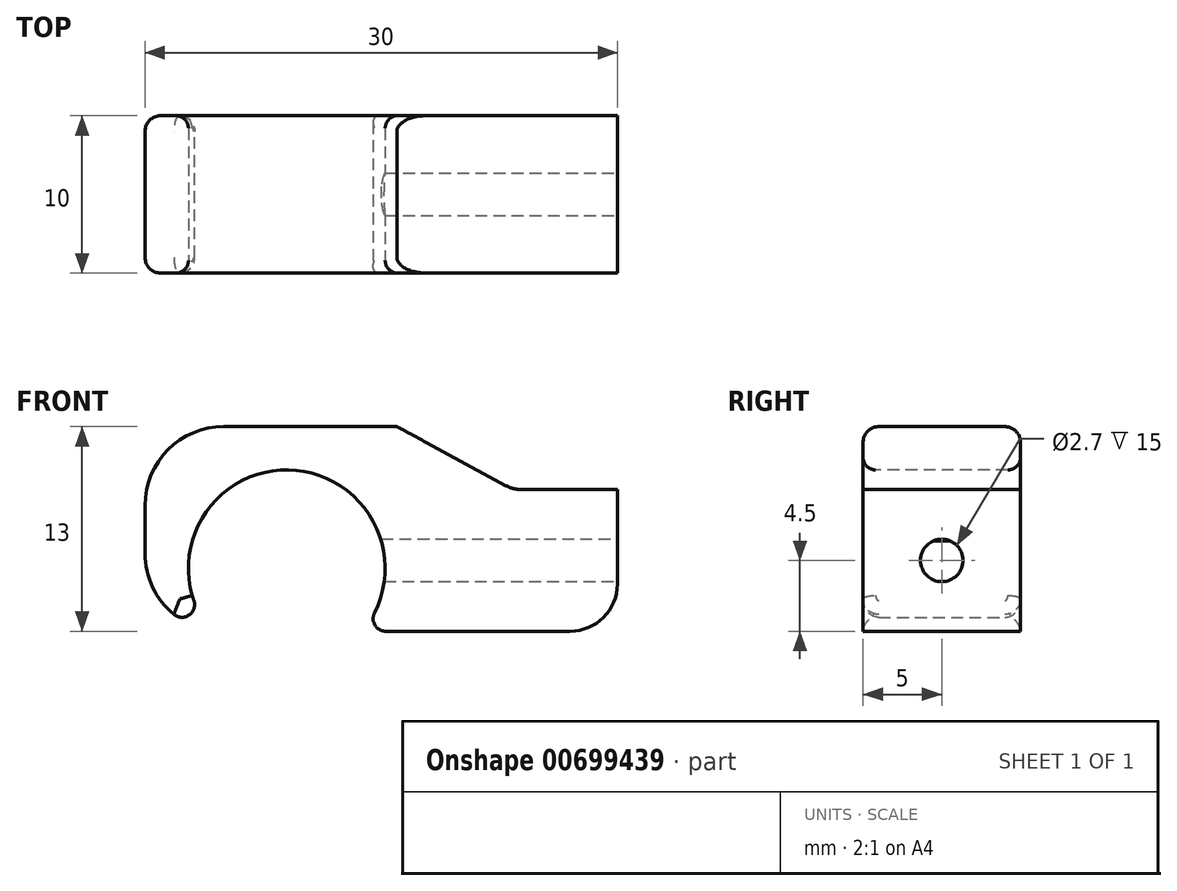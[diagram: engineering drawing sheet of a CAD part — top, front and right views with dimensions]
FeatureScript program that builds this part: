
annotation { "Feature Type Name" : "Feature", "Feature Type Description" : "" }
export const myFeature = defineFeature(function(context is Context, id is Id, definition is map)
    precondition{}
    {
        {
            var Q0;
            Q0=qCreatedBy(makeId("Top.planeOp"),FACE);
            var sketch = newSketch(context, id + "F0", { "sketchPlane" : qUnion([Q0])});
            skLineSegment(sketch, "E0.bottom", {"start": v(-15, 5) * mm, "end": v(15, 5) * mm});
            skLineSegment(sketch, "E0.top", {"start": v(-15, -5) * mm, "end": v(15, -5) * mm});
            skLineSegment(sketch, "E0.left", {"start": v(-15, 5) * mm, "end": v(-15, -5) * mm});
            skLineSegment(sketch, "E0.right", {"start": v(15, 5) * mm, "end": v(15, -5) * mm});
            skSolve(sketch);
        }
        {
            var Q0;
            Q0=makeQuery(id+"F0.imprint","IMPRINT",FACE,{"disambiguationData":[TD([[makeQuery(id+"F0.imprint","IMPRINT",EDGE,{"derivedFrom":sQuery(id+"F0.wireOp",EDGE,"E0.bottom")}),-1.0]])]});
            extrude(context, id + "F1", {"entities" : qUnion([Q0]), "depth" : 13 * mm, "offsetDistance" : 25 * mm});
        }
        {
            var Q0;
            Q0=makeQuery(id+"F1.opExtrude","SWEPT_FACE",FACE,{"disambiguationData":[OSD([sQuery(id+"F0.wireOp",EDGE,"E0.top")])]});
            var sketch = newSketch(context, id + "F2", { "sketchPlane" : qUnion([Q0])});
            skCircle(sketch, "E1", {"center": v(-6, 4) * mm, "radius": 6.25 * mm});
            skSolve(sketch);
        }
        {
            var Q0;
            Q0 = qSketchRegion(id + "F2", true);
            extrude(context, id + "F3", {"entities" : qUnion([Q0]), "operationType" : NewBodyOperationType.REMOVE, "endBound" : BoundingType.THROUGH_ALL, "oppositeDirection" : true, "depth" : 25 * mm, "offsetDistance" : 25 * mm});
        }
        {
            var Q0;
            Q0=makeQuery(id+"F1.opExtrude","CAP_EDGE",EDGE,{"disambiguationData":[OSD([sQuery(id+"F0.wireOp",EDGE,"E0.left")])],"isStart":false});
            var Q1;
            Q1=makeQuery(id+"F1.opExtrude","CAP_EDGE",EDGE,{"disambiguationData":[OSD([sQuery(id+"F0.wireOp",EDGE,"E0.left")])],"isStart":true});
            fillet(context, id + "F4", {"entities" : qUnion([Q0, Q1]), "radius" : 5 * mm, "tangentPropagation" : true, "allowEdgeOverflow" : false});
        }
        {
            var Q0;
            Q0=makeQuery(id+"F1.opExtrude","SWEPT_FACE",FACE,{"disambiguationData":[OSD([sQuery(id+"F0.wireOp",EDGE,"E0.top")])]});
            var sketch = newSketch(context, id + "F5", { "sketchPlane" : qUnion([Q0])});
            skLineSegment(sketch, "E2.bottom", {"start": v(15, 13) * mm, "end": v(1, 13) * mm});
            skLineSegment(sketch, "E2.top", {"start": v(15, 9) * mm, "end": v(8.38, 9) * mm});
            skLineSegment(sketch, "E2.left", {"start": v(15, 13) * mm, "end": v(15, 9) * mm});
            skLineSegment(sketch, "E3", {"start": v(1, 13) * mm, "end": v(8.38, 9) * mm});
            skSolve(sketch);
        }
        {
            var Q0;
            Q0 = qSketchRegion(id + "F5", true);
            extrude(context, id + "F6", {"entities" : qUnion([Q0]), "operationType" : NewBodyOperationType.REMOVE, "endBound" : BoundingType.THROUGH_ALL, "oppositeDirection" : true, "depth" : 25 * mm, "offsetDistance" : 25 * mm});
        }
        {
            var Q0;
            Q0=makeQuery(id+"F6.boolean.opBoolean","COPY",EDGE,{"derivedFrom":makeQuery(id+"F6.opExtrude","SWEPT_EDGE",EDGE,{"disambiguationData":[OSD([sQuery(id+"F0.wireOp",EDGE,"E0.top"),sQuery(id+"F5.wireOp",EDGE,"E2.bottom"),sQuery(id+"F5.wireOp",EDGE,"E2.right")])]})});
            var Q1;
            Q1=makeQuery(id+"F6.boolean.opBoolean","COPY",EDGE,{"derivedFrom":makeQuery(id+"F6.opExtrude","SWEPT_EDGE",EDGE,{"disambiguationData":[OSD([sQuery(id+"F5.wireOp",EDGE,"E2.top"),sQuery(id+"F5.wireOp",EDGE,"E2.right")])]})});
            fillet(context, id + "F7", {"entities" : qUnion([Q0, Q1]), "radius" : 2 * mm, "tangentPropagation" : true, "allowEdgeOverflow" : false});
        }
        {
            var Q0;
            Q0=makeQuery(id+"F6.boolean.opBoolean","COPY",EDGE,{"derivedFrom":makeQuery(id+"F6.opExtrude","SWEPT_EDGE",EDGE,{"disambiguationData":[OSD([sQuery(id+"F0.wireOp",EDGE,"E0.top"),sQuery(id+"F0.wireOp",EDGE,"E0.right"),sQuery(id+"F5.wireOp",EDGE,"E2.top"),sQuery(id+"F5.wireOp",EDGE,"E2.left")])]})});
            var Q1;
            Q1=makeQuery(id+"F1.opExtrude","CAP_EDGE",EDGE,{"disambiguationData":[OSD([sQuery(id+"F0.wireOp",EDGE,"E0.right")])],"isStart":true});
            fillet(context, id + "F8", {"entities" : qUnion([Q0, Q1]), "radius" : 3 * mm, "tangentPropagation" : true, "allowEdgeOverflow" : false});
        }
        {
            var Q0;
            Q0=makeQuery(id+"F1.opExtrude","SWEPT_FACE",FACE,{"disambiguationData":[OSD([sQuery(id+"F0.wireOp",EDGE,"E0.right")])]});
            var sketch = newSketch(context, id + "F9", { "sketchPlane" : qUnion([Q0])});
            skCircle(sketch, "E4", {"center": v(0, 4.5) * mm, "radius": 1.35 * mm});
            skSolve(sketch);
        }
        {
            var Q0;
            Q0=makeQuery(id+"F9.imprint","IMPRINT",FACE,{"disambiguationData":[TD([[makeQuery(id+"F9.imprint","IMPRINT",EDGE,{"derivedFrom":sQuery(id+"F9.wireOp",EDGE,"E4")}),1.0]])]});
            extrude(context, id + "F10", {"entities" : qUnion([Q0]), "operationType" : NewBodyOperationType.REMOVE, "oppositeDirection" : true, "depth" : 15 * mm, "offsetDistance" : 25 * mm});
        }
        {
            var Q0;
            Q0=makeQuery(id+"F1.opExtrude","CAP_EDGE",EDGE,{"disambiguationData":[OSD([sQuery(id+"F0.wireOp",EDGE,"E0.top")])],"isStart":false});
            var Q1;
            Q1=makeQuery(id+"F1.opExtrude","CAP_EDGE",EDGE,{"disambiguationData":[OSD([sQuery(id+"F0.wireOp",EDGE,"E0.bottom")])],"isStart":false});
            fillet(context, id + "F11", {"entities" : qUnion([Q0, Q1]), "radius" : 1 * mm, "tangentPropagation" : true, "allowEdgeOverflow" : false});
        }
        {
            var Q0;
            Q0=makeQuery(id+"F4.opFillet","BLEND_EDGE",EDGE,{"blendedFrom":[makeQuery(id+"F1.opExtrude","CAP_EDGE",EDGE,{"disambiguationData":[OSD([sQuery(id+"F0.wireOp",EDGE,"E0.left")])],"isStart":true}),makeQuery(id+"F3.boolean.opBoolean","COPY",FACE,{"derivedFrom":makeQuery(id+"F3.opExtrude","SWEPT_FACE",FACE,{"disambiguationData":[OSD([sQuery(id+"F2.wireOp",EDGE,"E1")])]})})],"blendedInto":[makeQuery(id+"F3.boolean.opBoolean","COPY",FACE,{"derivedFrom":makeQuery(id+"F3.opExtrude","SWEPT_FACE",FACE,{"disambiguationData":[OSD([sQuery(id+"F2.wireOp",EDGE,"E1")])]})})]});
            var Q1;
            Q1=makeQuery(id+"F3.boolean.opBoolean","INTERSECT",EDGE,{"disambiguationData":[OD(1.0)],"derivedFrom":[makeQuery(id+"F1.opExtrude","CAP_FACE",FACE,{"disambiguationData":[OSD([sQuery(id+"F0.wireOp",EDGE,"E0.bottom"),sQuery(id+"F0.wireOp",EDGE,"E0.top"),sQuery(id+"F0.wireOp",EDGE,"E0.left"),sQuery(id+"F0.wireOp",EDGE,"E0.right")])],"isStart":true}),makeQuery(id+"F3.opExtrude","SWEPT_FACE",FACE,{"disambiguationData":[OSD([sQuery(id+"F2.wireOp",EDGE,"E1")])]})]});
            fillet(context, id + "F12", {"entities" : qUnion([Q0, Q1]), "radius" : 0.8 * mm, "tangentPropagation" : true, "allowEdgeOverflow" : false});
        }
    });
